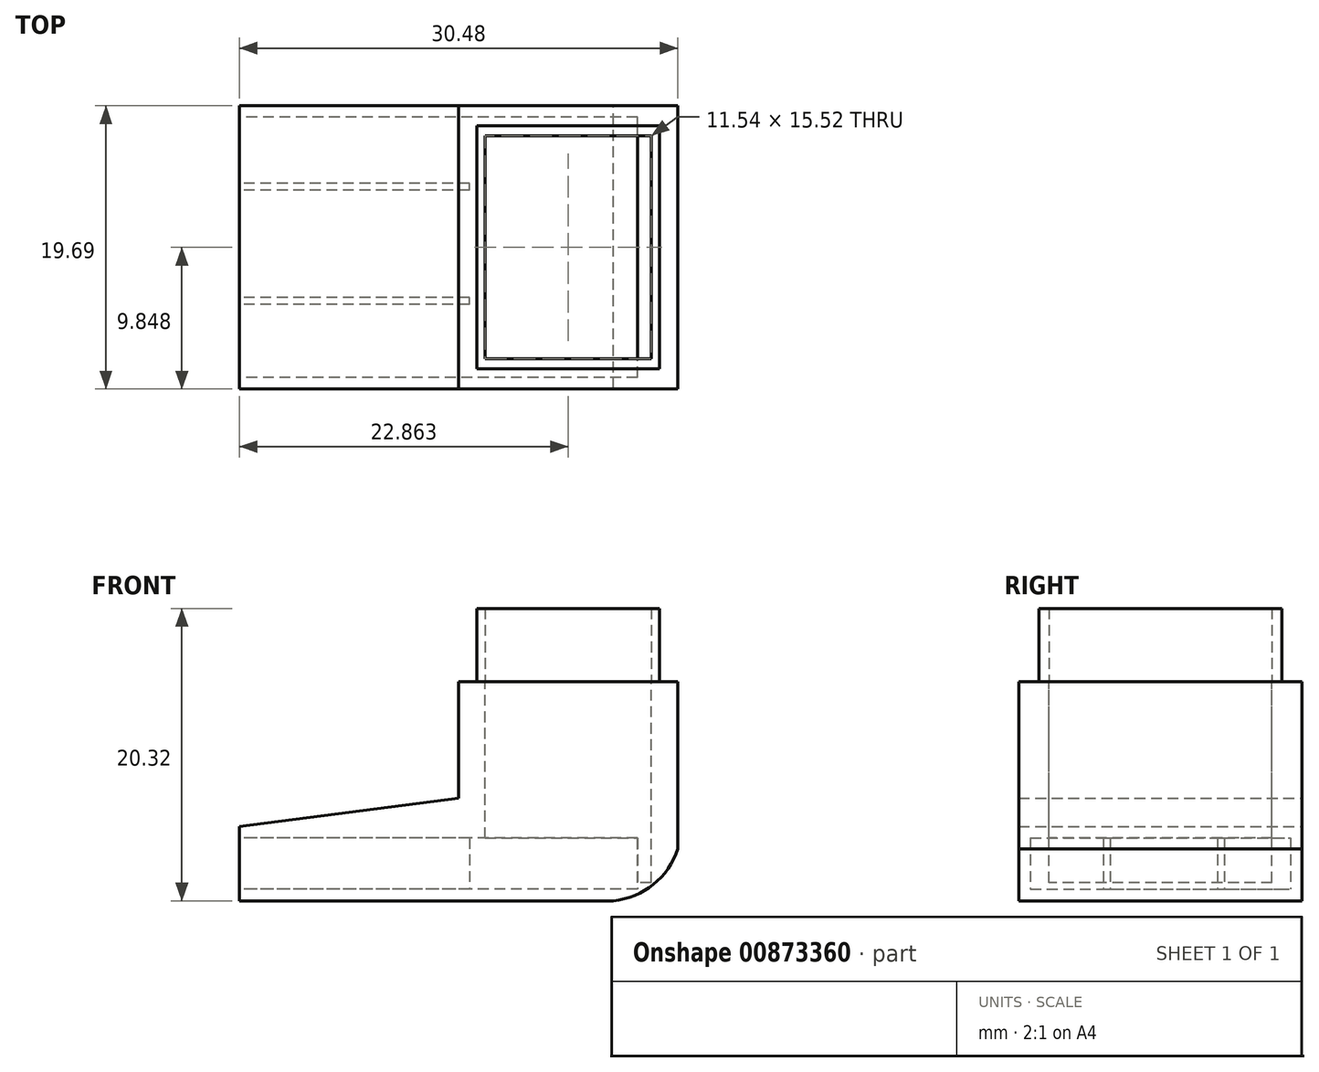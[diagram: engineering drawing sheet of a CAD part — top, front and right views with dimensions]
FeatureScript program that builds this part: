
annotation { "Feature Type Name" : "Feature", "Feature Type Description" : "" }
export const myFeature = defineFeature(function(context is Context, id is Id, definition is map)
    precondition{}
    {
        {
            var Q0;
            Q0=qCreatedBy(makeId("Front.planeOp"),FACE);
            var sketch = newSketch(context, id + "F0", { "sketchPlane" : qUnion([Q0])});
            skLineSegment(sketch, "E0.bottom", {"start": v(-69.69, 0) * mm, "end": v(-39.2, 0) * mm, "construction": true});
            skLineSegment(sketch, "E0.top", {"start": v(-69.69, 15.24) * mm, "end": v(-39.2, 15.24) * mm, "construction": true});
            skLineSegment(sketch, "E0.left", {"start": v(-69.69, 0) * mm, "end": v(-69.69, 15.24) * mm, "construction": true});
            skLineSegment(sketch, "E0.right", {"start": v(-39.2, 0) * mm, "end": v(-39.2, 15.24) * mm, "construction": true});
            skLineSegment(sketch, "E1", {"start": v(-69.69, 0) * mm, "end": v(-69.69, 5.16) * mm});
            skLineSegment(sketch, "E2", {"start": v(-69.69, 5.16) * mm, "end": v(-54.45, 7.14) * mm});
            skLineSegment(sketch, "E3", {"start": v(-54.45, 7.14) * mm, "end": v(-54.45, 15.24) * mm});
            skLineSegment(sketch, "E4", {"start": v(-54.45, 15.24) * mm, "end": v(-39.2, 15.24) * mm});
            skArc(sketch, "E5", {"start": v(-43.68, 0) * mm, "mid": v(-40.9, 1.14) * mm, "end": v(-39.2, 3.6) * mm});
            skLineSegment(sketch, "E6", {"start": v(-69.69, 0) * mm, "end": v(-43.68, 0) * mm});
            skLineSegment(sketch, "E7", {"start": v(-39.2, 15.24) * mm, "end": v(-39.2, 3.6) * mm});
            skSolve(sketch);
        }
        {
            var Q0;
            Q0 = qSketchRegion(id + "F0", true);
            extrude(context, id + "F1", {"entities" : qUnion([Q0]), "depth" : 19.68 * mm, "offsetDistance" : 25.4 * mm});
        }
        {
            var Q0;
            Q0=makeQuery(id+"F1.opExtrude","SWEPT_FACE",FACE,{"disambiguationData":[OSD([sQuery(id+"F0.wireOp",EDGE,"E4")])]});
            var sketch = newSketch(context, id + "F2", { "sketchPlane" : qUnion([Q0])});
            skLineSegment(sketch, "E8.bottom", {"start": v(-41.05, -17.6) * mm, "end": v(-52.6, -17.6) * mm});
            skLineSegment(sketch, "E8.top", {"start": v(-41.05, -2.08) * mm, "end": v(-52.6, -2.08) * mm});
            skLineSegment(sketch, "E8.left", {"start": v(-41.05, -17.6) * mm, "end": v(-41.05, -2.08) * mm});
            skLineSegment(sketch, "E8.right", {"start": v(-52.6, -17.6) * mm, "end": v(-52.6, -2.08) * mm});
            skPoint(sketch, "E8.middle", {"position": v(-46.83, -9.84) * mm});
            skPoint(sketch, "E8.middle.positionSnap0", {"position": v(-46.83, -19.69) * mm});
            skPoint(sketch, "E8.middle.positionSnap1", {"position": v(-54.45, -9.84) * mm});
            skPoint(sketch, "E8.centerSnap0", {"position": v(-46.83, -19.69) * mm});
            skPoint(sketch, "E8.centerSnap1", {"position": v(-54.45, -9.84) * mm});
            skSolve(sketch);
        }
        {
            var Q0;
            Q0 = qSketchRegion(id + "F2", true);
            extrude(context, id + "F3", {"entities" : qUnion([Q0]), "operationType" : NewBodyOperationType.REMOVE, "oppositeDirection" : true, "depth" : 13.97 * mm, "offsetDistance" : 25.4 * mm});
        }
        {
            var Q0;
            Q0=makeQuery(id+"F1.opExtrude","SWEPT_FACE",FACE,{"disambiguationData":[OSD([sQuery(id+"F0.wireOp",EDGE,"E1")])]});
            var sketch = newSketch(context, id + "F4", { "sketchPlane" : qUnion([Q0])});
            skLineSegment(sketch, "E9.bottom", {"start": v(18.88, 4.36) * mm, "end": v(0.8, 4.36) * mm});
            skLineSegment(sketch, "E9.top", {"start": v(18.88, 0.8) * mm, "end": v(0.8, 0.8) * mm});
            skLineSegment(sketch, "E9.left", {"start": v(18.88, 4.36) * mm, "end": v(18.88, 0.8) * mm});
            skLineSegment(sketch, "E9.right", {"start": v(0.8, 4.36) * mm, "end": v(0.8, 0.8) * mm});
            skPoint(sketch, "E9.middle", {"position": v(9.84, 2.58) * mm});
            skPoint(sketch, "E9.middle.positionSnap0", {"position": v(9.84, 0) * mm});
            skPoint(sketch, "E9.middle.positionSnap1", {"position": v(0, 2.58) * mm});
            skPoint(sketch, "E9.centerSnap0", {"position": v(9.84, 0) * mm});
            skPoint(sketch, "E9.centerSnap1", {"position": v(0, 2.58) * mm});
            skSolve(sketch);
        }
        {
            var Q0;
            Q0 = qSketchRegion(id + "F4", true);
            extrude(context, id + "F5", {"entities" : qUnion([Q0]), "operationType" : NewBodyOperationType.REMOVE, "oppositeDirection" : true, "depth" : 27.7 * mm, "offsetDistance" : 25.4 * mm});
        }
        {
            var Q0;
            Q0=makeQuery(id+"F1.opExtrude","SWEPT_FACE",FACE,{"disambiguationData":[OSD([sQuery(id+"F0.wireOp",EDGE,"E4")])]});
            var sketch = newSketch(context, id + "F6", { "sketchPlane" : qUnion([Q0])});
            skPoint(sketch, "E10.middle", {"position": v(-46.83, -9.84) * mm});
            skPoint(sketch, "E10.middle.positionSnap0", {"position": v(-46.83, -17.6) * mm});
            skPoint(sketch, "E10.middle.positionSnap1", {"position": v(-41.05, -9.84) * mm});
            skPoint(sketch, "E10.centerSnap0", {"position": v(-46.83, -17.6) * mm});
            skPoint(sketch, "E10.centerSnap1", {"position": v(-41.05, -9.84) * mm});
            skLineSegment(sketch, "E11.bottom", {"start": v(-41.05, -17.6) * mm, "end": v(-52.6, -17.6) * mm});
            skLineSegment(sketch, "E11.top", {"start": v(-41.05, -2.08) * mm, "end": v(-52.6, -2.08) * mm});
            skLineSegment(sketch, "E11.left", {"start": v(-41.05, -17.6) * mm, "end": v(-41.05, -2.08) * mm});
            skLineSegment(sketch, "E11.right", {"start": v(-52.6, -17.6) * mm, "end": v(-52.6, -2.08) * mm});
            skLineSegment(sketch, "E12.bottom", {"start": v(-40.47, -18.29) * mm, "end": v(-53.18, -18.29) * mm});
            skLineSegment(sketch, "E12.top", {"start": v(-40.47, -1.4) * mm, "end": v(-53.18, -1.4) * mm});
            skLineSegment(sketch, "E12.left", {"start": v(-40.47, -18.29) * mm, "end": v(-40.47, -1.4) * mm});
            skLineSegment(sketch, "E12.right", {"start": v(-53.18, -18.29) * mm, "end": v(-53.18, -1.4) * mm});
            skSolve(sketch);
        }
        {
            var Q0;
            Q0 = qSketchRegion(id + "F6", true);
            extrude(context, id + "F7", {"entities" : qUnion([Q0]), "depth" : 5.08 * mm, "offsetDistance" : 25.4 * mm});
        }
        {
            var Q0;
            Q0=makeQuery(id+"F1.opExtrude","SWEPT_FACE",FACE,{"disambiguationData":[OSD([sQuery(id+"F0.wireOp",EDGE,"E1")])]});
            var sketch = newSketch(context, id + "F8", { "sketchPlane" : qUnion([Q0])});
            skLineSegment(sketch, "E13.bottom", {"start": v(5.4, 4.36) * mm, "end": v(5.88, 4.36) * mm});
            skLineSegment(sketch, "E13.top", {"start": v(5.4, 0.8) * mm, "end": v(5.88, 0.8) * mm});
            skLineSegment(sketch, "E13.left", {"start": v(5.88, 4.36) * mm, "end": v(5.88, 0.8) * mm});
            skLineSegment(sketch, "E13.right", {"start": v(5.4, 4.36) * mm, "end": v(5.4, 0.8) * mm});
            skLineSegment(sketch, "E14.bottom", {"start": v(13.8, 4.36) * mm, "end": v(13.32, 4.36) * mm});
            skLineSegment(sketch, "E14.top", {"start": v(13.8, 0.8) * mm, "end": v(13.32, 0.8) * mm});
            skLineSegment(sketch, "E14.left", {"start": v(13.32, 4.36) * mm, "end": v(13.32, 0.8) * mm});
            skLineSegment(sketch, "E14.right", {"start": v(13.8, 4.36) * mm, "end": v(13.8, 0.8) * mm});
            skSolve(sketch);
        }
        {
            var Q0;
            Q0 = qSketchRegion(id + "F8", true);
            extrude(context, id + "F9", {"entities" : qUnion([Q0]), "operationType" : NewBodyOperationType.ADD, "oppositeDirection" : true, "depth" : 16 * mm, "offsetDistance" : 25.4 * mm});
        }
    });
